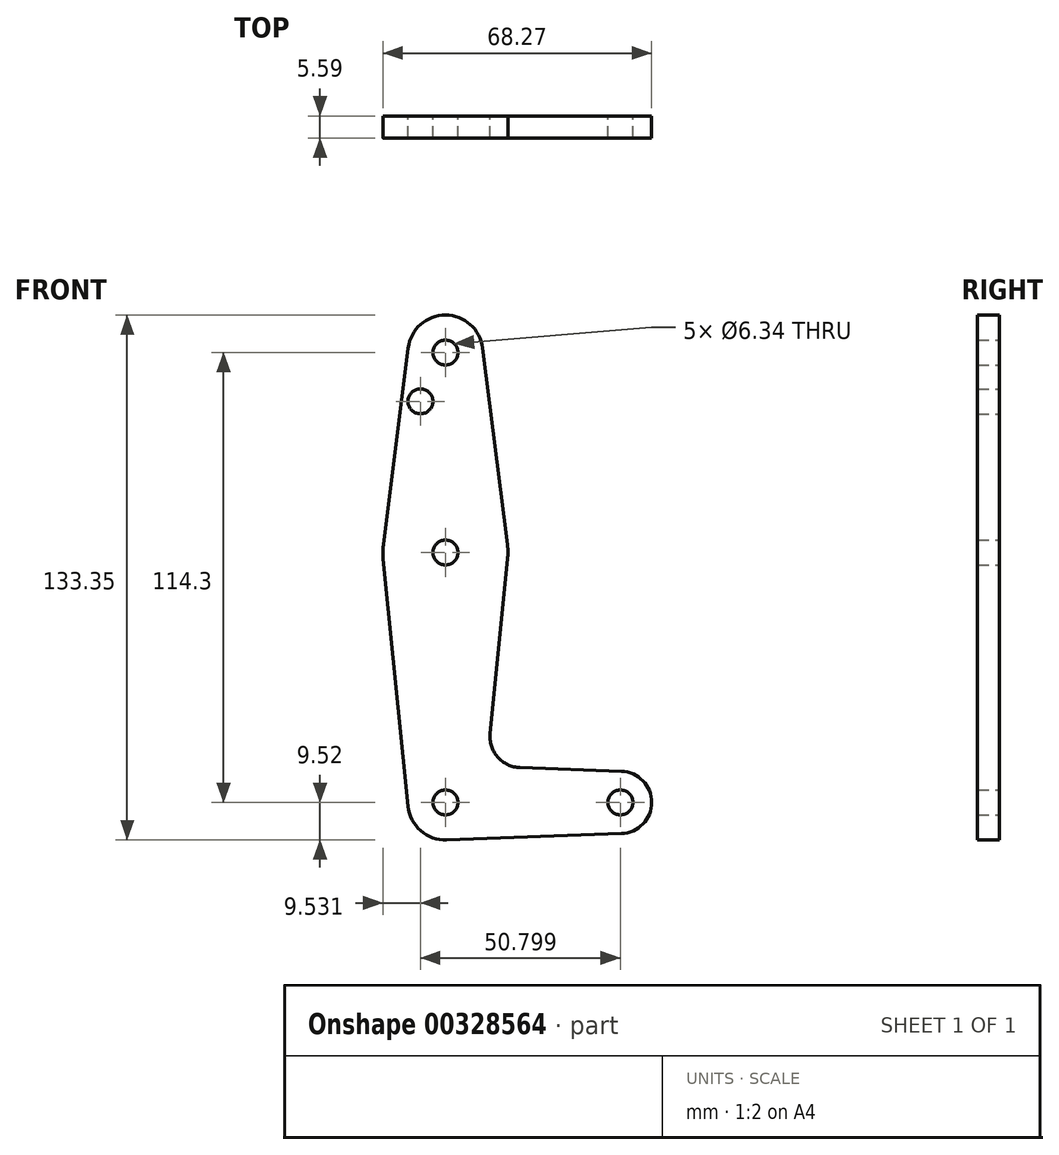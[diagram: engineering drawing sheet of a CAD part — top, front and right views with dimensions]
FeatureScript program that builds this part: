
annotation { "Feature Type Name" : "Feature", "Feature Type Description" : "" }
export const myFeature = defineFeature(function(context is Context, id is Id, definition is map)
    precondition{}
    {
        {
            var Q0;
            Q0=qCreatedBy(makeId("Front.planeOp"),FACE);
            var sketch = newSketch(context, id + "F0", { "sketchPlane" : qUnion([Q0])});
            skLineSegment(sketch, "E0", {"start": v(0, 114.3) * mm, "end": v(0, 0) * mm, "construction": true});
            skLineSegment(sketch, "E1", {"start": v(0, 0) * mm, "end": v(44.45, 0) * mm, "construction": true});
            skCircle(sketch, "E2", {"center": v(0, 114.3) * mm, "radius": 9.53 * mm});
            skCircle(sketch, "E3", {"center": v(0, 0) * mm, "radius": 9.53 * mm});
            skCircle(sketch, "E4", {"center": v(44.45, 0) * mm, "radius": 7.94 * mm});
            skCircle(sketch, "E5", {"center": v(0, 63.5) * mm, "radius": 15.88 * mm});
            skLineSegment(sketch, "E6", {"start": v(-9.45, 115.5) * mm, "end": v(-15.75, 65.48) * mm});
            skLineSegment(sketch, "E7", {"start": v(9.45, 115.5) * mm, "end": v(15.75, 65.48) * mm});
            skLineSegment(sketch, "E8", {"start": v(-15.8, 61.91) * mm, "end": v(-9.48, -0.95) * mm});
            skLineSegment(sketch, "E9", {"start": v(15.8, 61.91) * mm, "end": v(11.34, 17.59) * mm});
            skLineSegment(sketch, "E10", {"start": v(18.97, 8.85) * mm, "end": v(44.73, 7.93) * mm});
            skLineSegment(sketch, "E11", {"start": v(0.34, -9.52) * mm, "end": v(44.73, -7.93) * mm});
            skCircle(sketch, "E12", {"center": v(0, 114.3) * mm, "radius": 3.17 * mm});
            skCircle(sketch, "E13", {"center": v(0, 63.5) * mm, "radius": 3.17 * mm});
            skCircle(sketch, "E14", {"center": v(0, 0) * mm, "radius": 3.17 * mm});
            skCircle(sketch, "E15", {"center": v(-6.35, 101.9) * mm, "radius": 3.17 * mm});
            skCircle(sketch, "E16", {"center": v(44.45, 0) * mm, "radius": 3.17 * mm});
            skArc(sketch, "E17.filletArc", {"start": v(11.34, 17.59) * mm, "mid": v(13.26, 11.57) * mm, "end": v(18.97, 8.85) * mm});
            skSolve(sketch);
        }
        {
            var Q0;
            Q0 = qSketchRegion(id + "F0", true);
            extrude(context, id + "F1", {"entities" : qUnion([Q0]), "depth" : 5.6 * mm});
        }
    });
